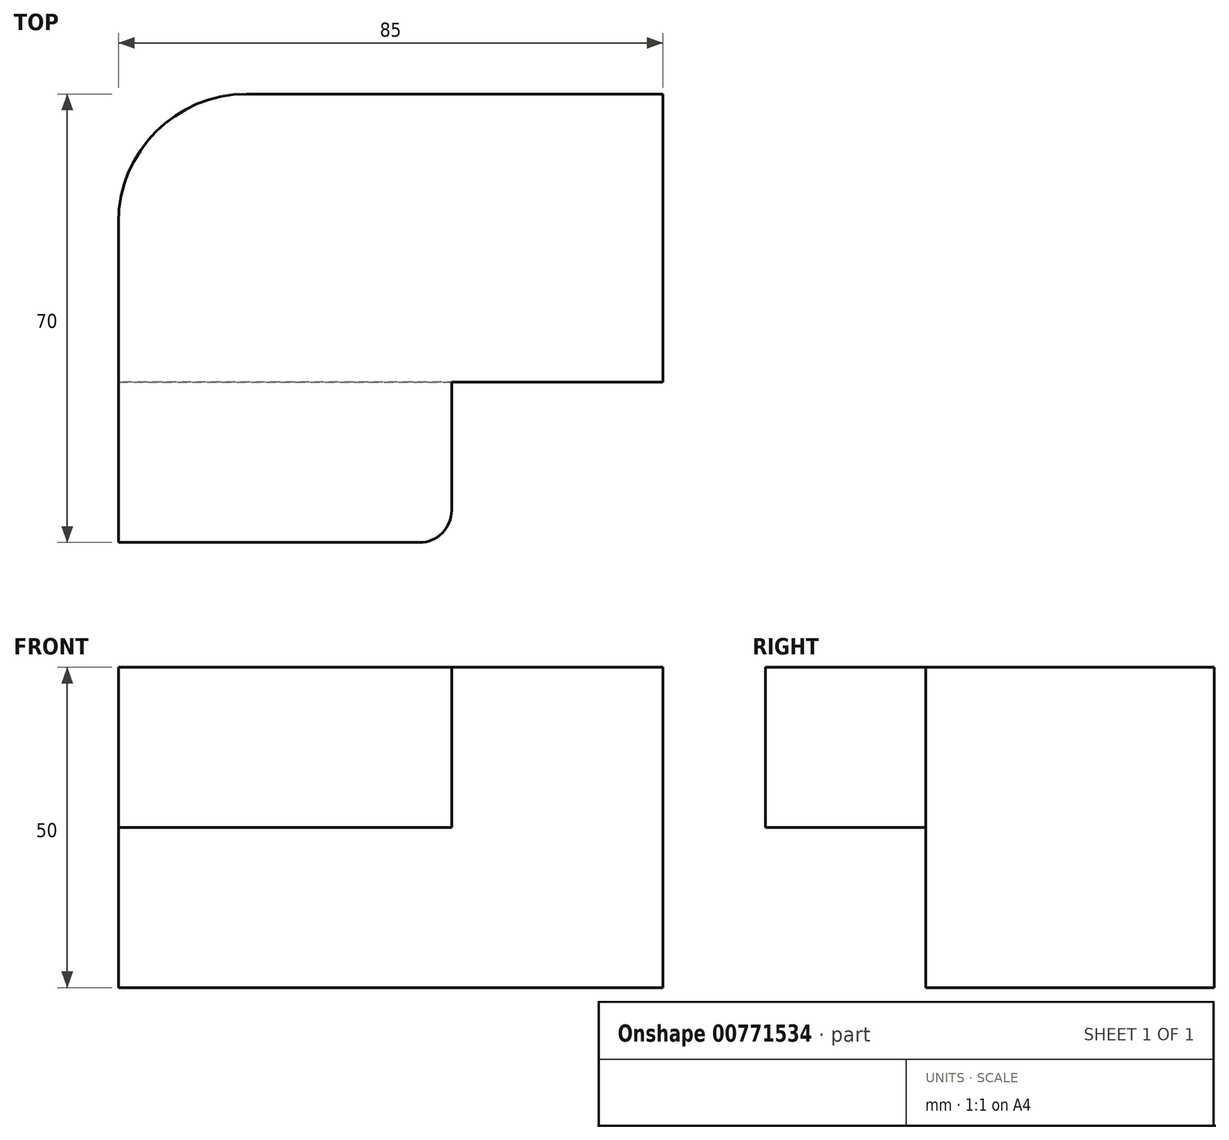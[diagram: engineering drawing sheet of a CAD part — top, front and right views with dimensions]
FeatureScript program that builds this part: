
annotation { "Feature Type Name" : "Feature", "Feature Type Description" : "" }
export const myFeature = defineFeature(function(context is Context, id is Id, definition is map)
    precondition{}
    {
        {
            var Q0;
            Q0=qCreatedBy(makeId("Top.planeOp"),FACE);
            var sketch = newSketch(context, id + "F0", { "sketchPlane" : qUnion([Q0])});
            skLineSegment(sketch, "E0.bottom", {"start": v(42.5, 22.5) * mm, "end": v(-42.5, 22.5) * mm});
            skLineSegment(sketch, "E0.top", {"start": v(42.5, -22.5) * mm, "end": v(-42.5, -22.5) * mm});
            skLineSegment(sketch, "E0.left", {"start": v(42.5, 22.5) * mm, "end": v(42.5, -22.5) * mm});
            skLineSegment(sketch, "E0.right", {"start": v(-42.5, 22.5) * mm, "end": v(-42.5, -22.5) * mm});
            skPoint(sketch, "E0.middle", {"position": v(0, 0) * mm});
            skSolve(sketch);
        }
        {
            var Q0;
            Q0=makeQuery(id+"F0.imprint","IMPRINT",FACE,{"disambiguationData":[TD([[makeQuery(id+"F0.imprint","IMPRINT",EDGE,{"derivedFrom":sQuery(id+"F0.wireOp",EDGE,"E0.bottom")}),1.0]])]});
            extrude(context, id + "F1", {"entities" : qUnion([Q0]), "depth" : 50 * mm, "offsetDistance" : 25 * mm});
        }
        {
            var Q0;
            Q0=makeQuery(id+"F1.opExtrude","SWEPT_EDGE",EDGE,{"disambiguationData":[OSD([sQuery(id+"F0.wireOp",EDGE,"E0.bottom"),sQuery(id+"F0.wireOp",EDGE,"E0.right")])]});
            fillet(context, id + "F2", {"entities" : qUnion([Q0]), "radius" : 20 * mm, "tangentPropagation" : true, "allowEdgeOverflow" : false});
        }
        {
            var Q0;
            Q0=makeQuery(id+"F1.opExtrude","SWEPT_FACE",FACE,{"disambiguationData":[OSD([sQuery(id+"F0.wireOp",EDGE,"E0.top")])]});
            var sketch = newSketch(context, id + "F3", { "sketchPlane" : qUnion([Q0])});
            skLineSegment(sketch, "E1.bottom", {"start": v(-42.5, 50) * mm, "end": v(9.5, 50) * mm});
            skLineSegment(sketch, "E1.top", {"start": v(-42.5, 25) * mm, "end": v(9.5, 25) * mm});
            skLineSegment(sketch, "E1.left", {"start": v(-42.5, 50) * mm, "end": v(-42.5, 25) * mm});
            skLineSegment(sketch, "E1.right", {"start": v(9.5, 50) * mm, "end": v(9.5, 25) * mm});
            skSolve(sketch);
        }
        {
            var Q0;
            Q0=makeQuery(id+"F3.imprint","IMPRINT",FACE,{"disambiguationData":[TD([[makeQuery(id+"F3.imprint","IMPRINT",EDGE,{"derivedFrom":sQuery(id+"F3.wireOp",EDGE,"E1.bottom")}),1.0]])]});
            extrude(context, id + "F4", {"entities" : qUnion([Q0]), "operationType" : NewBodyOperationType.ADD, "depth" : 25 * mm, "offsetDistance" : 25 * mm});
        }
        {
            var Q0;
            Q0=makeQuery(id+"F4.opExtrude","CAP_EDGE",EDGE,{"disambiguationData":[OSD([sQuery(id+"F3.wireOp",EDGE,"E1.right")])],"isStart":false});
            fillet(context, id + "F5", {"entities" : qUnion([Q0]), "radius" : 5 * mm, "tangentPropagation" : true, "allowEdgeOverflow" : false});
        }
    });
